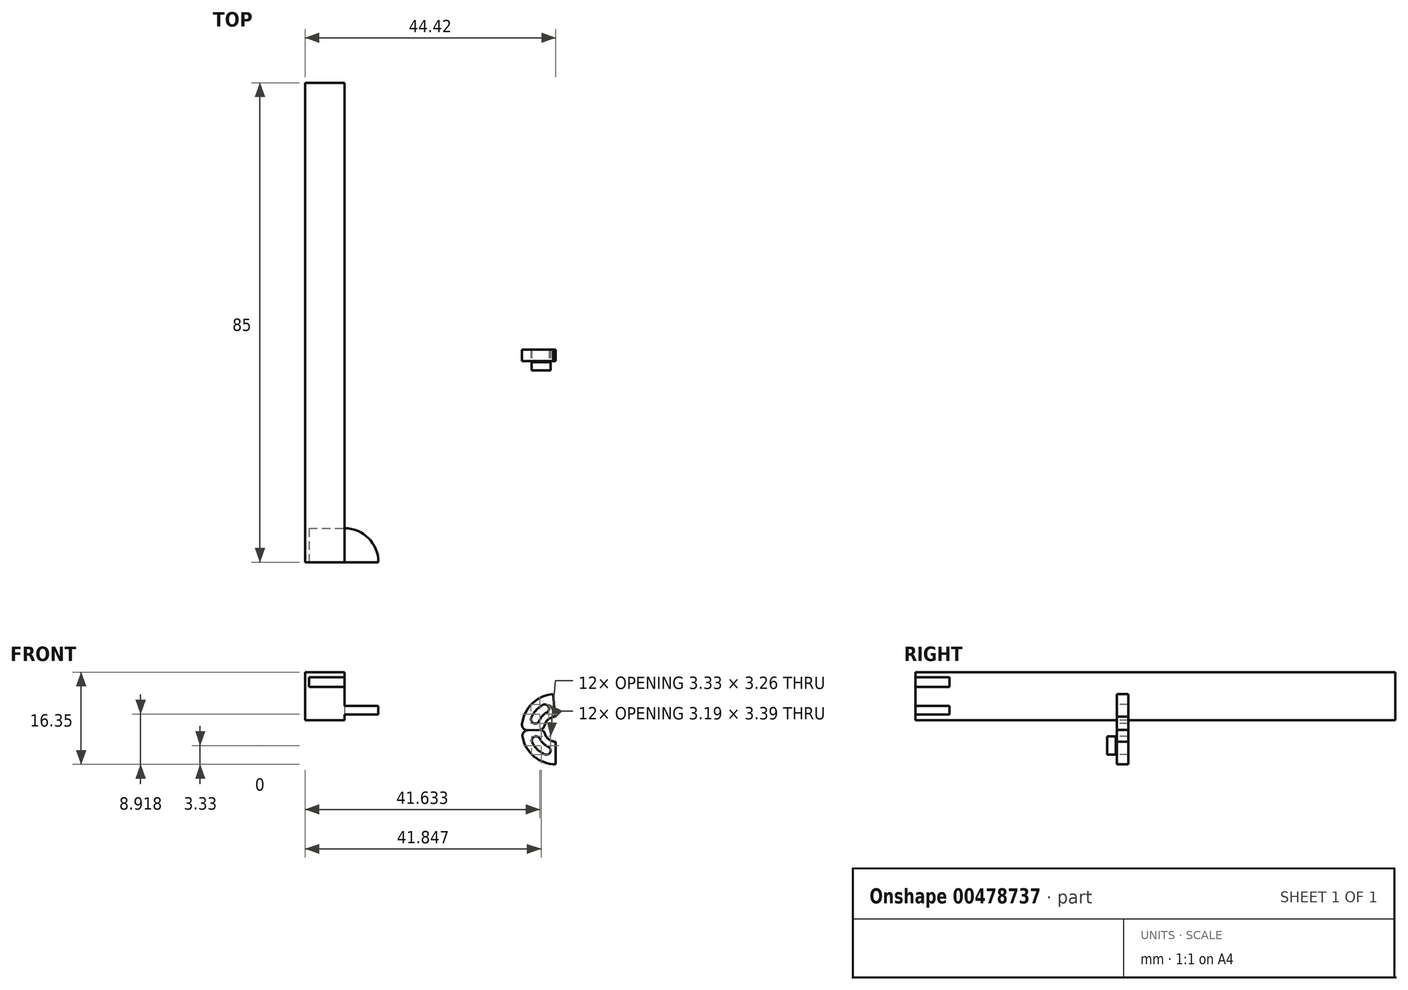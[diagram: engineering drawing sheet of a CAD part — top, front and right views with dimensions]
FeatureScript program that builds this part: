
annotation { "Feature Type Name" : "Feature", "Feature Type Description" : "" }
export const myFeature = defineFeature(function(context is Context, id is Id, definition is map)
    precondition{}
    {
        {
            var Q0;
            Q0=qCreatedBy(makeId("Top.planeOp"),FACE);
            var sketch = newSketch(context, id + "F0", { "sketchPlane" : qUnion([Q0])});
            skLineSegment(sketch, "E0.bottom", {"start": v(-51.06, 49.31) * mm, "end": v(-44.06, 49.31) * mm});
            skLineSegment(sketch, "E0.top", {"start": v(-51.06, -35.69) * mm, "end": v(-44.06, -35.69) * mm});
            skLineSegment(sketch, "E0.left", {"start": v(-51.06, 49.31) * mm, "end": v(-51.06, -35.69) * mm});
            skLineSegment(sketch, "E0.right", {"start": v(-44.06, 49.31) * mm, "end": v(-44.06, -35.69) * mm});
            skLineSegment(sketch, "E1", {"start": v(-44.06, -35.69) * mm, "end": v(-38.06, -35.69) * mm});
            skArc(sketch, "E2", {"start": v(-38.06, -35.69) * mm, "mid": v(-39.82, -31.44) * mm, "end": v(-44.06, -29.69) * mm});
            skSolve(sketch);
        }
        {
            var Q0;
            {var subQ1=sQuery(id+"F0.wireOp",EDGE,"E0.bottom");Q0=makeQuery(id+"F0.imprint","IMPRINT",FACE,{"disambiguationData":[TD([[makeQuery(id+"F0.imprint","IMPRINT",EDGE,{"derivedFrom":subQ1}),-1.0]])]});}
            extrude(context, id + "F1", {"entities" : qUnion([Q0]), "depth" : 8.5 * mm});
        }
        {
            var Q0;
            {var subQ0=sQuery(id+"F0.wireOp",EDGE,"E1");Q0=makeQuery(id+"F0.imprint","IMPRINT",FACE,{"disambiguationData":[TD([[makeQuery(id+"F0.imprint","IMPRINT",EDGE,{"derivedFrom":subQ0}),1.0]])]});}
            cPlane(context, id + "F2", {"entities" : qUnion([Q0]), "cplaneType" : CPlaneType.OFFSET, "offset" : 1 * mm, "width" : 150 * mm, "height" : 150 * mm});
        }
        {
            var Q0;
            Q0=qCreatedBy(id+"F2.planeOp",FACE);
            var sketch = newSketch(context, id + "F3", { "sketchPlane" : qUnion([Q0])});
            skLineSegment(sketch, "E3.0.0", {"start": v(-44.06, -29.69) * mm, "end": v(-44.06, -35.69) * mm});
            skLineSegment(sketch, "E3.0.1", {"start": v(-44.06, -35.69) * mm, "end": v(-38.06, -35.69) * mm});
            skArc(sketch, "E3.0.2", {"start": v(-38.06, -35.69) * mm, "mid": v(-39.82, -31.44) * mm, "end": v(-44.06, -29.69) * mm});
            skSolve(sketch);
        }
        {
            var Q0;
            Q0 = qSketchRegion(id + "F3", true);
            extrude(context, id + "F4", {"entities" : qUnion([Q0]), "operationType" : NewBodyOperationType.ADD, "depth" : 1.5 * mm});
        }
        {
            var Q0;
            Q0=makeQuery(id+"F1.opExtrude","SWEPT_FACE",FACE,{"disambiguationData":[OSD([sQuery(id+"F0.wireOp",EDGE,"E0.right")])]});
            var sketch = newSketch(context, id + "F5", { "sketchPlane" : qUnion([Q0])});
            skLineSegment(sketch, "E4", {"start": v(-35.69, 6.75) * mm, "end": v(-27.57, 6.75) * mm, "construction": true});
            skLineSegment(sketch, "E5.bottom", {"start": v(-29.69, 5.9) * mm, "end": v(-35.69, 5.9) * mm});
            skLineSegment(sketch, "E5.top", {"start": v(-29.69, 7.6) * mm, "end": v(-35.69, 7.6) * mm});
            skLineSegment(sketch, "E5.left", {"start": v(-29.69, 5.9) * mm, "end": v(-29.69, 7.6) * mm});
            skLineSegment(sketch, "E5.right", {"start": v(-35.69, 5.9) * mm, "end": v(-35.69, 7.6) * mm});
            skPoint(sketch, "E5.middle", {"position": v(-32.69, 6.75) * mm});
            skPoint(sketch, "E5.middle.positionSnap0", {"position": v(-32.69, 2.5) * mm});
            skPoint(sketch, "E5.centerSnap0", {"position": v(-32.69, 2.5) * mm});
            skSolve(sketch);
        }
        {
            var Q0;
            Q0 = qSketchRegion(id + "F5", true);
            extrude(context, id + "F6", {"entities" : qUnion([Q0]), "operationType" : NewBodyOperationType.REMOVE, "oppositeDirection" : true, "depth" : 6.3 * mm});
        }
        {
            var Q0;
            Q0=qCreatedBy(makeId("Front.planeOp"),FACE);
            var sketch = newSketch(context, id + "F7", { "sketchPlane" : qUnion([Q0])});
            skArc(sketch, "E6", {"start": v(-12.53, -3) * mm, "mid": v(-10.45, -6.48) * mm, "end": v(-6.64, -7.85) * mm});
            skLineSegment(sketch, "E7", {"start": v(-6.64, -1.85) * mm, "end": v(-6.64, -8.93) * mm, "construction": true});
            skLineSegment(sketch, "E8", {"start": v(-8.64, -3.15) * mm, "end": v(-8.64, 0) * mm, "construction": true});
            skArc(sketch, "E9", {"start": v(-8.55, -2.44) * mm, "mid": v(-7.83, -3.46) * mm, "end": v(-6.64, -3.85) * mm});
            skLineSegment(sketch, "E10", {"start": v(-6.64, -7.85) * mm, "end": v(-6.64, -3.85) * mm});
            skLineSegment(sketch, "E11", {"start": v(-9.54, -1.73) * mm, "end": v(-11.58, -1.8) * mm});
            skCircle(sketch, "E12", {"center": v(-6.64, -1.85) * mm, "radius": 3.92 * mm, "construction": true});
            skArc(sketch, "E13.0", {"start": v(-10.8, -3.98) * mm, "mid": v(-9.88, -5.21) * mm, "end": v(-8.61, -6.08) * mm});
            skArc(sketch, "E14.0", {"start": v(-9.46, -3.3) * mm, "mid": v(-8.84, -4.13) * mm, "end": v(-7.98, -4.72) * mm});
            skLineSegment(sketch, "E15", {"start": v(-6.64, -1.85) * mm, "end": v(-9.69, -8.38) * mm, "construction": true});
            skLineSegment(sketch, "E16", {"start": v(-6.64, -1.85) * mm, "end": v(-12.82, -5.02) * mm, "construction": true});
            skArc(sketch, "E17", {"start": v(-8.61, -6.08) * mm, "mid": v(-7.62, -5.72) * mm, "end": v(-7.98, -4.72) * mm});
            skArc(sketch, "E18", {"start": v(-10.8, -3.98) * mm, "mid": v(-10.47, -2.97) * mm, "end": v(-9.46, -3.3) * mm});
            skPoint(sketch, "E19.visualSharp", {"position": v(-8.63, -1.7) * mm});
            skArc(sketch, "E19.filletArc", {"start": v(-8.55, -2.44) * mm, "mid": v(-8.93, -1.92) * mm, "end": v(-9.54, -1.73) * mm});
            skPoint(sketch, "E20.visualSharp", {"position": v(-12.64, -1.85) * mm});
            skArc(sketch, "E20.filletArc", {"start": v(-12.64, -1.85) * mm, "mid": v(-12.64, -1.85) * mm, "end": v(-12.64, -1.85) * mm});
            skArc(sketch, "E21", {"start": v(-6.64, -7.85) * mm, "mid": v(-2.4, 2.4) * mm, "end": v(-12.64, -1.85) * mm, "construction": true});
            skPoint(sketch, "E22", {"position": v(-10.56, -1.77) * mm});
            skPoint(sketch, "E23.newPointA", {"position": v(-11.58, -1.8) * mm});
            skArc(sketch, "E23.filletArc", {"start": v(-11.58, -1.8) * mm, "mid": v(-12.33, -2.19) * mm, "end": v(-12.53, -3) * mm});
            skSolve(sketch);
        }
        {
            var Q0;
            Q0=makeQuery(id+"F7.imprint","IMPRINT",FACE,{"disambiguationData":[TD([[makeQuery(id+"F7.imprint","IMPRINT",EDGE,{"derivedFrom":sQuery(id+"F7.wireOp",EDGE,"E6")}),1.0]])]});
            extrude(context, id + "F8", {"entities" : qUnion([Q0]), "oppositeDirection" : true, "depth" : 2 * mm});
        }
        {
            var Q0;
            Q0=makeQuery(id+"F8.opExtrude","CAP_FACE",FACE,{"disambiguationData":[OSD([sQuery(id+"F7.wireOp",EDGE,"E6"),sQuery(id+"F7.wireOp",EDGE,"E9"),sQuery(id+"F7.wireOp",EDGE,"E10"),sQuery(id+"F7.wireOp",EDGE,"E11"),sQuery(id+"F7.wireOp",EDGE,"E13.0"),sQuery(id+"F7.wireOp",EDGE,"E14.0"),sQuery(id+"F7.wireOp",EDGE,"E17"),sQuery(id+"F7.wireOp",EDGE,"E18"),sQuery(id+"F7.wireOp",EDGE,"E19.filletArc"),sQuery(id+"F7.wireOp",EDGE,"E23.filletArc")])],"isStart":true});
            cPlane(context, id + "F9", {"entities" : qUnion([Q0]), "cplaneType" : CPlaneType.OFFSET, "offset" : .2 * mm, "width" : 150 * mm, "height" : 150 * mm});
        }
        {
            var Q0;
            Q0=qCreatedBy(id+"F9.planeOp",FACE);
            var sketch = newSketch(context, id + "F10", { "sketchPlane" : qUnion([Q0])});
            skArc(sketch, "E24.0.0", {"start": v(-7.98, -4.72) * mm, "mid": v(-8.84, -4.13) * mm, "end": v(-9.46, -3.3) * mm});
            skArc(sketch, "E24.0.1", {"start": v(-9.46, -3.3) * mm, "mid": v(-10.47, -2.97) * mm, "end": v(-10.8, -3.98) * mm});
            skArc(sketch, "E24.0.2", {"start": v(-10.8, -3.98) * mm, "mid": v(-9.88, -5.21) * mm, "end": v(-8.61, -6.08) * mm});
            skArc(sketch, "E24.0.3", {"start": v(-8.61, -6.08) * mm, "mid": v(-7.62, -5.72) * mm, "end": v(-7.98, -4.72) * mm});
            skArc(sketch, "E25.0", {"start": v(-8.4, -2.8) * mm, "mid": v(-8.07, -3.24) * mm, "end": v(-7.64, -3.58) * mm});
            skArc(sketch, "E25.1", {"start": v(-11.9, -4.71) * mm, "mid": v(-10.94, -6.03) * mm, "end": v(-9.64, -7.04) * mm});
            skLineSegment(sketch, "E26", {"start": v(-6.64, -5.3) * mm, "end": v(-6.64, -5.3) * mm});
            skPoint(sketch, "E27.visualSharp", {"position": v(-6.64, -7.85) * mm});
            skArc(sketch, "E27.filletArc", {"start": v(-9.64, -7.04) * mm, "mid": v(-6.9, -6.3) * mm, "end": v(-7.64, -3.58) * mm});
            skPoint(sketch, "E28.visualSharp", {"position": v(-6.64, -3.85) * mm});
            skArc(sketch, "E29.filletArc", {"start": v(-8.4, -2.8) * mm, "mid": v(-11.1, -2) * mm, "end": v(-11.9, -4.71) * mm});
            skSolve(sketch);
        }
        {
            var Q0;
            Q0=makeQuery(id+"F10.imprint","IMPRINT",FACE,{"disambiguationData":[TD([[makeQuery(id+"F10.imprint","IMPRINT",EDGE,{"derivedFrom":sQuery(id+"F10.wireOp",EDGE,"E24.0.0")}),-1.0]])]});
            extrude(context, id + "F11", {"entities" : qUnion([Q0]), "depth" : 1.5 * mm});
        }
        {
            var Q0;
            Q0=makeQuery(id+"F8.opExtrude","SWEPT_BODY",BODY,{"disambiguationData":[OSD([sQuery(id+"F7.wireOp",EDGE,"E6"),sQuery(id+"F7.wireOp",EDGE,"E9"),sQuery(id+"F7.wireOp",EDGE,"E10"),sQuery(id+"F7.wireOp",EDGE,"E11"),sQuery(id+"F7.wireOp",EDGE,"E13.0"),sQuery(id+"F7.wireOp",EDGE,"E14.0"),sQuery(id+"F7.wireOp",EDGE,"E17"),sQuery(id+"F7.wireOp",EDGE,"E18"),sQuery(id+"F7.wireOp",EDGE,"E19.filletArc"),sQuery(id+"F7.wireOp",EDGE,"E23.filletArc")])]});
            var Q1;
            Q1=makeQuery(id+"F8.opExtrude","SWEPT_FACE",FACE,{"disambiguationData":[OSD([sQuery(id+"F7.wireOp",EDGE,"E11")])]});
            mirror(context, id + "F12", {"entities" : qUnion([Q0]), "mirrorPlane" : qUnion([Q1])});
        }
    });
